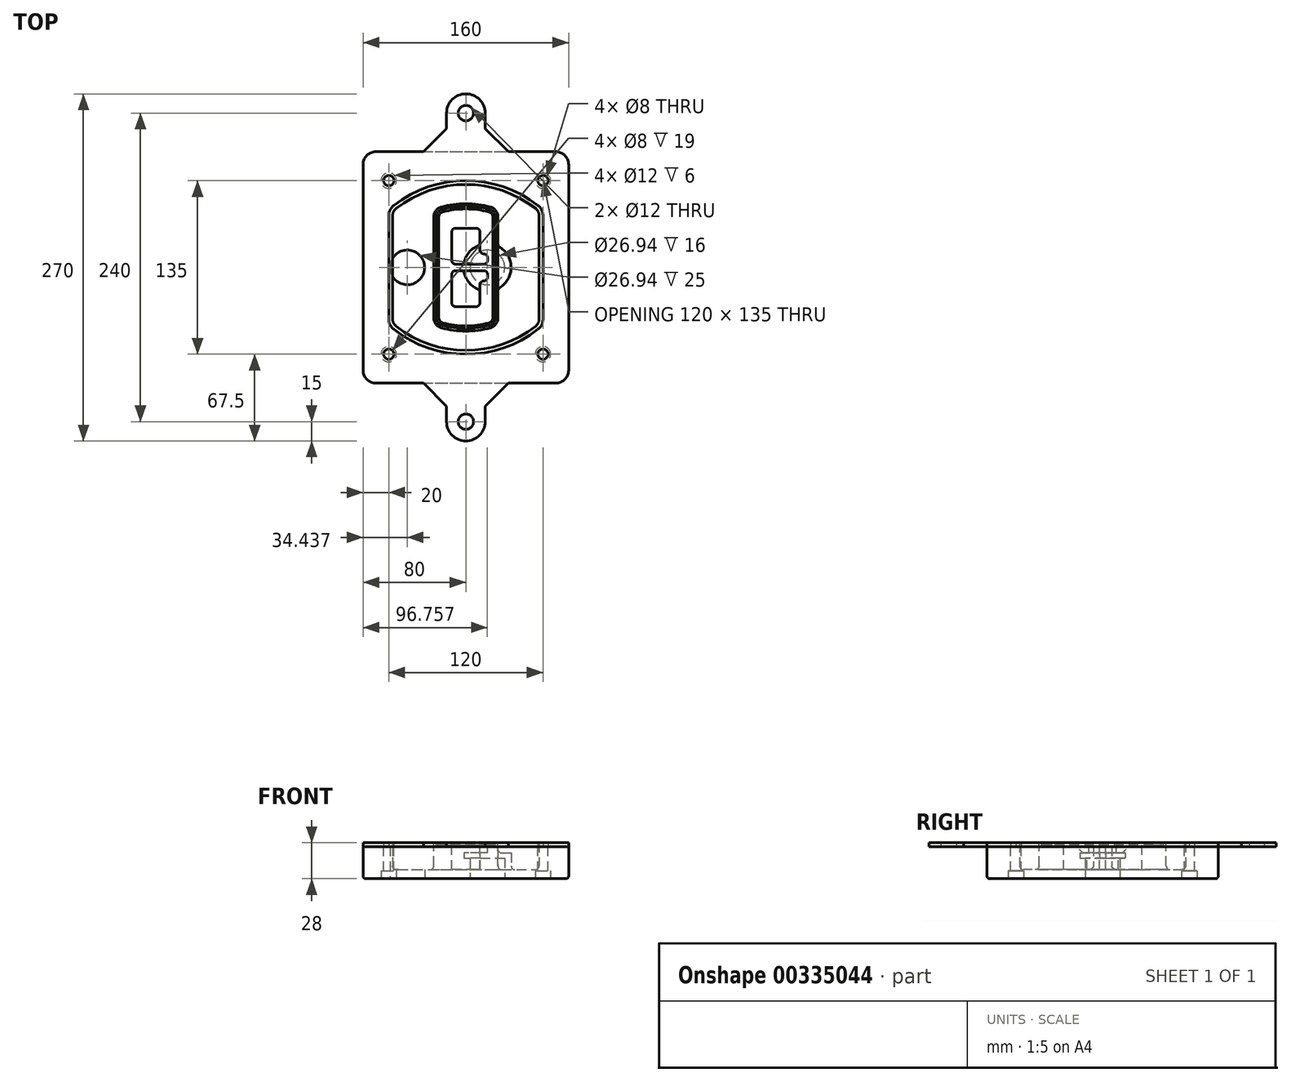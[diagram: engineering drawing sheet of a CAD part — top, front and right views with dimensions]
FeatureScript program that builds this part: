
annotation { "Feature Type Name" : "Feature", "Feature Type Description" : "" }
export const myFeature = defineFeature(function(context is Context, id is Id, definition is map)
    precondition{}
    {
        {
            var Q0;
            Q0=qCreatedBy(makeId("Top.planeOp"),FACE);
            var sketch = newSketch(context, id + "F0", { "sketchPlane" : qUnion([Q0])});
            skPoint(sketch, "E0.rect.middle", {"position": v(0, 0) * mm});
            skLineSegment(sketch, "E1.bottom", {"start": v(-70, -90) * mm, "end": v(70, -90) * mm});
            skLineSegment(sketch, "E1.top", {"start": v(-70, 90) * mm, "end": v(70, 90) * mm});
            skLineSegment(sketch, "E1.left", {"start": v(-80, -80) * mm, "end": v(-80, 80) * mm});
            skLineSegment(sketch, "E1.right", {"start": v(80, -80) * mm, "end": v(80, 80) * mm});
            skLineSegment(sketch, "E2", {"start": v(-80, 90) * mm, "end": v(80, -90) * mm, "construction": true});
            skLineSegment(sketch, "E3", {"start": v(80, 90) * mm, "end": v(-80, -90) * mm, "construction": true});
            skCircle(sketch, "E4", {"center": v(-60, 67.5) * mm, "radius": 4 * mm});
            skCircle(sketch, "E5", {"center": v(60, 67.5) * mm, "radius": 4 * mm});
            skCircle(sketch, "E6", {"center": v(60, -67.5) * mm, "radius": 4 * mm});
            skCircle(sketch, "E7", {"center": v(-60, -67.5) * mm, "radius": 4 * mm});
            skLineSegment(sketch, "E8", {"start": v(-60, 67.5) * mm, "end": v(60, 67.5) * mm, "construction": true});
            skLineSegment(sketch, "E9", {"start": v(60, 67.5) * mm, "end": v(60, -67.5) * mm, "construction": true});
            skLineSegment(sketch, "E10", {"start": v(60, -67.5) * mm, "end": v(-60, -67.5) * mm, "construction": true});
            skLineSegment(sketch, "E11", {"start": v(-60, -67.5) * mm, "end": v(-60, 67.5) * mm, "construction": true});
            skLineSegment(sketch, "E12", {"start": v(-60, 40.3) * mm, "end": v(-60, -40.3) * mm});
            skLineSegment(sketch, "E13", {"start": v(60, 40.3) * mm, "end": v(60, -40.3) * mm});
            skArc(sketch, "E14", {"start": v(56.15, 48.18) * mm, "mid": v(0, 67.5) * mm, "end": v(-56.15, 48.18) * mm});
            skArc(sketch, "E15", {"start": v(-56.15, -48.18) * mm, "mid": v(0, -67.5) * mm, "end": v(56.15, -48.18) * mm});
            skLineSegment(sketch, "E16", {"start": v(-60, 0) * mm, "end": v(60, 0) * mm, "construction": true});
            skPoint(sketch, "E17.visualSharp", {"position": v(-60, -45) * mm});
            skArc(sketch, "E17.filletArc", {"start": v(-60, -40.3) * mm, "mid": v(-58.99, -44.68) * mm, "end": v(-56.15, -48.18) * mm});
            skPoint(sketch, "E18.visualSharp", {"position": v(-60, 45) * mm});
            skArc(sketch, "E18.filletArc", {"start": v(-56.15, 48.18) * mm, "mid": v(-58.99, 44.68) * mm, "end": v(-60, 40.3) * mm});
            skPoint(sketch, "E19.visualSharp", {"position": v(60, 45) * mm});
            skArc(sketch, "E19.filletArc", {"start": v(60, 40.3) * mm, "mid": v(58.99, 44.68) * mm, "end": v(56.15, 48.18) * mm});
            skPoint(sketch, "E20.visualSharp", {"position": v(60, -45) * mm});
            skArc(sketch, "E20.filletArc", {"start": v(56.15, -48.18) * mm, "mid": v(58.99, -44.68) * mm, "end": v(60, -40.3) * mm});
            skPoint(sketch, "E21.visualSharp", {"position": v(-80, 90) * mm});
            skArc(sketch, "E21.filletArc", {"start": v(-70, 90) * mm, "mid": v(-77.07, 87.07) * mm, "end": v(-80, 80) * mm});
            skPoint(sketch, "E22.visualSharp", {"position": v(80, 90) * mm});
            skArc(sketch, "E22.filletArc", {"start": v(80, 80) * mm, "mid": v(77.07, 87.07) * mm, "end": v(70, 90) * mm});
            skPoint(sketch, "E23.visualSharp", {"position": v(80, -90) * mm});
            skArc(sketch, "E23.filletArc", {"start": v(70, -90) * mm, "mid": v(77.07, -87.07) * mm, "end": v(80, -80) * mm});
            skPoint(sketch, "E24.visualSharp", {"position": v(-80, -90) * mm});
            skArc(sketch, "E24.filletArc", {"start": v(-80, -80) * mm, "mid": v(-77.07, -87.07) * mm, "end": v(-70, -90) * mm});
            skArc(sketch, "E25.0", {"start": v(57, 40.3) * mm, "mid": v(56.3, 43.36) * mm, "end": v(54.3, 45.81) * mm});
            skLineSegment(sketch, "E25.1", {"start": v(57, 40.3) * mm, "end": v(57, -40.3) * mm});
            skArc(sketch, "E25.2", {"start": v(54.3, -45.81) * mm, "mid": v(56.3, -43.36) * mm, "end": v(57, -40.3) * mm});
            skArc(sketch, "E25.3", {"start": v(-54.3, -45.81) * mm, "mid": v(0, -64.5) * mm, "end": v(54.3, -45.81) * mm});
            skArc(sketch, "E25.4", {"start": v(-57, -40.3) * mm, "mid": v(-56.3, -43.36) * mm, "end": v(-54.3, -45.81) * mm});
            skArc(sketch, "E25.5", {"start": v(54.3, 45.81) * mm, "mid": v(0, 64.5) * mm, "end": v(-54.3, 45.81) * mm});
            skLineSegment(sketch, "E25.6", {"start": v(-57, 40.3) * mm, "end": v(-57, -40.3) * mm});
            skArc(sketch, "E25.7", {"start": v(-54.3, 45.81) * mm, "mid": v(-56.3, 43.36) * mm, "end": v(-57, 40.3) * mm});
            skArc(sketch, "E26.0", {"start": v(-58.62, 51.33) * mm, "mid": v(-62.58, 46.43) * mm, "end": v(-64, 40.3) * mm});
            skArc(sketch, "E26.1", {"start": v(58.62, 51.33) * mm, "mid": v(0, 71.5) * mm, "end": v(-58.62, 51.33) * mm});
            skArc(sketch, "E26.2", {"start": v(64, 40.3) * mm, "mid": v(62.58, 46.43) * mm, "end": v(58.62, 51.33) * mm});
            skLineSegment(sketch, "E26.3", {"start": v(64, 40.3) * mm, "end": v(64, -40.3) * mm});
            skArc(sketch, "E26.4", {"start": v(58.62, -51.33) * mm, "mid": v(62.58, -46.43) * mm, "end": v(64, -40.3) * mm});
            skLineSegment(sketch, "E26.5", {"start": v(-64, 40.3) * mm, "end": v(-64, -40.3) * mm});
            skArc(sketch, "E26.6", {"start": v(-58.62, -51.33) * mm, "mid": v(0, -71.5) * mm, "end": v(58.62, -51.33) * mm});
            skArc(sketch, "E26.7", {"start": v(-64, -40.3) * mm, "mid": v(-62.58, -46.43) * mm, "end": v(-58.62, -51.33) * mm});
            skSolve(sketch);
        }
        {
            var Q0;
            Q0=makeQuery(id+"F0.imprint","IMPRINT",FACE,{"disambiguationData":[TD([[makeQuery(id+"F0.imprint","IMPRINT",EDGE,{"derivedFrom":sQuery(id+"F0.wireOp",EDGE,"E1.bottom")}),1.0]])]});
            var Q1;
            Q1=makeQuery(id+"F0.imprint","IMPRINT",FACE,{"disambiguationData":[TD([[makeQuery(id+"F0.imprint","IMPRINT",EDGE,{"derivedFrom":sQuery(id+"F0.wireOp",EDGE,"E12")}),1.0]])]});
            var Q2;
            Q2=makeQuery(id+"F0.imprint","IMPRINT",FACE,{"disambiguationData":[TD([[makeQuery(id+"F0.imprint","IMPRINT",EDGE,{"derivedFrom":sQuery(id+"F0.wireOp",EDGE,"E25.0")}),1.0]])]});
            var Q3;
            Q3=makeQuery(id+"F0.imprint","IMPRINT",FACE,{"disambiguationData":[TD([[makeQuery(id+"F0.imprint","IMPRINT",EDGE,{"derivedFrom":sQuery(id+"F0.wireOp",EDGE,"E12")}),-1.0]])]});
            extrude(context, id + "F1", {"entities" : qUnion([Q0, Q1, Q2, Q3]), "oppositeDirection" : true, "depth" : 25 * mm});
        }
        {
            var Q0;
            Q0=makeQuery(id+"F0.imprint","IMPRINT",FACE,{"disambiguationData":[TD([[makeQuery(id+"F0.imprint","IMPRINT",EDGE,{"derivedFrom":sQuery(id+"F0.wireOp",EDGE,"E12")}),1.0]])]});
            extrude(context, id + "F2", {"entities" : qUnion([Q0]), "operationType" : NewBodyOperationType.ADD, "depth" : 3 * mm});
        }
        {
            var Q0;
            Q0=makeQuery(id+"F0.imprint","IMPRINT",FACE,{"disambiguationData":[TD([[makeQuery(id+"F0.imprint","IMPRINT",EDGE,{"derivedFrom":sQuery(id+"F0.wireOp",EDGE,"E25.0")}),1.0]])]});
            extrude(context, id + "F3", {"entities" : qUnion([Q0]), "operationType" : NewBodyOperationType.REMOVE, "oppositeDirection" : true, "depth" : 18 * mm});
        }
        {
            var Q0;
            Q0=makeQuery(id+"F2.opExtrude","CAP_FACE",FACE,{"disambiguationData":[OSD([sQuery(id+"F0.wireOp",EDGE,"E12"),sQuery(id+"F0.wireOp",EDGE,"E13"),sQuery(id+"F0.wireOp",EDGE,"E14"),sQuery(id+"F0.wireOp",EDGE,"E15"),sQuery(id+"F0.wireOp",EDGE,"E17.filletArc"),sQuery(id+"F0.wireOp",EDGE,"E18.filletArc"),sQuery(id+"F0.wireOp",EDGE,"E19.filletArc"),sQuery(id+"F0.wireOp",EDGE,"E20.filletArc"),sQuery(id+"F0.wireOp",EDGE,"E25.0"),sQuery(id+"F0.wireOp",EDGE,"E25.1"),sQuery(id+"F0.wireOp",EDGE,"E25.2"),sQuery(id+"F0.wireOp",EDGE,"E25.3"),sQuery(id+"F0.wireOp",EDGE,"E25.4"),sQuery(id+"F0.wireOp",EDGE,"E25.5"),sQuery(id+"F0.wireOp",EDGE,"E25.6"),sQuery(id+"F0.wireOp",EDGE,"E25.7")])],"isStart":false});
            var sketch = newSketch(context, id + "F4", { "sketchPlane" : qUnion([Q0])});
            skArc(sketch, "E27.0", {"start": v(-19.08, -46.97) * mm, "mid": v(0, -49.5) * mm, "end": v(19.08, -46.97) * mm});
            skArc(sketch, "E28.0", {"start": v(19.08, 46.97) * mm, "mid": v(0, 49.5) * mm, "end": v(-19.08, 46.97) * mm});
            skLineSegment(sketch, "E29", {"start": v(-25, 39.25) * mm, "end": v(-25, -39.25) * mm});
            skLineSegment(sketch, "E30", {"start": v(25, 39.25) * mm, "end": v(25, -39.25) * mm});
            skLineSegment(sketch, "E31", {"start": v(-25, 45.1) * mm, "end": v(25, 45.1) * mm, "construction": true});
            skLineSegment(sketch, "E32", {"start": v(-25, -45.1) * mm, "end": v(25, -45.1) * mm, "construction": true});
            skPoint(sketch, "E33.visualSharp", {"position": v(-25, 45.1) * mm});
            skArc(sketch, "E33.filletArc", {"start": v(-19.08, 46.97) * mm, "mid": v(-23.35, 44.11) * mm, "end": v(-25, 39.25) * mm});
            skPoint(sketch, "E34.visualSharp", {"position": v(25, 45.1) * mm});
            skArc(sketch, "E34.filletArc", {"start": v(25, 39.25) * mm, "mid": v(23.35, 44.11) * mm, "end": v(19.08, 46.97) * mm});
            skPoint(sketch, "E35.visualSharp", {"position": v(25, -45.1) * mm});
            skArc(sketch, "E35.filletArc", {"start": v(19.08, -46.97) * mm, "mid": v(23.35, -44.11) * mm, "end": v(25, -39.25) * mm});
            skPoint(sketch, "E36.visualSharp", {"position": v(-25, -45.1) * mm});
            skArc(sketch, "E36.filletArc", {"start": v(-25, -39.25) * mm, "mid": v(-23.35, -44.11) * mm, "end": v(-19.08, -46.97) * mm});
            skArc(sketch, "E37.0", {"start": v(54.3, 45.81) * mm, "mid": v(0, 64.5) * mm, "end": v(-54.3, 45.81) * mm});
            skArc(sketch, "E37.1", {"start": v(-54.3, 45.81) * mm, "mid": v(-56.3, 43.36) * mm, "end": v(-57, 40.3) * mm});
            skLineSegment(sketch, "E37.2", {"start": v(-57, 40.3) * mm, "end": v(-57, -40.3) * mm});
            skArc(sketch, "E37.3", {"start": v(-57, -40.3) * mm, "mid": v(-56.3, -43.36) * mm, "end": v(-54.3, -45.81) * mm});
            skArc(sketch, "E37.4", {"start": v(-54.3, -45.81) * mm, "mid": v(0, -64.5) * mm, "end": v(54.3, -45.81) * mm});
            skArc(sketch, "E37.5", {"start": v(54.3, -45.81) * mm, "mid": v(56.3, -43.36) * mm, "end": v(57, -40.3) * mm});
            skLineSegment(sketch, "E37.6", {"start": v(57, 40.3) * mm, "end": v(57, -40.3) * mm});
            skArc(sketch, "E37.7", {"start": v(57, 40.3) * mm, "mid": v(56.3, 43.36) * mm, "end": v(54.3, 45.81) * mm});
            skLineSegment(sketch, "E38.0", {"start": v(23, 39.25) * mm, "end": v(23, -39.25) * mm});
            skArc(sketch, "E38.1", {"start": v(18.56, -45.04) * mm, "mid": v(21.76, -42.9) * mm, "end": v(23, -39.25) * mm});
            skArc(sketch, "E38.2", {"start": v(-18.56, -45.04) * mm, "mid": v(0, -47.5) * mm, "end": v(18.56, -45.04) * mm});
            skArc(sketch, "E38.3", {"start": v(-23, -39.25) * mm, "mid": v(-21.76, -42.9) * mm, "end": v(-18.56, -45.04) * mm});
            skLineSegment(sketch, "E38.4", {"start": v(-23, 39.25) * mm, "end": v(-23, -39.25) * mm});
            skArc(sketch, "E38.5", {"start": v(23, 39.25) * mm, "mid": v(21.76, 42.9) * mm, "end": v(18.56, 45.04) * mm});
            skArc(sketch, "E38.6", {"start": v(-18.56, 45.04) * mm, "mid": v(-21.76, 42.9) * mm, "end": v(-23, 39.25) * mm});
            skArc(sketch, "E38.7", {"start": v(18.56, 45.04) * mm, "mid": v(0, 47.5) * mm, "end": v(-18.56, 45.04) * mm});
            skArc(sketch, "E39.0", {"start": v(21, 39.25) * mm, "mid": v(20.18, 41.68) * mm, "end": v(18.04, 43.1) * mm});
            skLineSegment(sketch, "E39.1", {"start": v(21, 39.25) * mm, "end": v(21, -39.25) * mm});
            skArc(sketch, "E39.2", {"start": v(18.04, -43.1) * mm, "mid": v(20.18, -41.68) * mm, "end": v(21, -39.25) * mm});
            skArc(sketch, "E39.3", {"start": v(-18.04, -43.1) * mm, "mid": v(0, -45.5) * mm, "end": v(18.04, -43.1) * mm});
            skArc(sketch, "E39.4", {"start": v(-21, -39.25) * mm, "mid": v(-20.18, -41.68) * mm, "end": v(-18.04, -43.1) * mm});
            skArc(sketch, "E39.5", {"start": v(18.04, 43.1) * mm, "mid": v(0, 45.5) * mm, "end": v(-18.04, 43.1) * mm});
            skLineSegment(sketch, "E39.6", {"start": v(-21, 39.25) * mm, "end": v(-21, -39.25) * mm});
            skArc(sketch, "E39.7", {"start": v(-18.04, 43.1) * mm, "mid": v(-20.18, 41.68) * mm, "end": v(-21, 39.25) * mm});
            skLineSegment(sketch, "E40", {"start": v(-25, 0) * mm, "end": v(25, 0) * mm, "construction": true});
            skLineSegment(sketch, "E41", {"start": v(-11, 5.5) * mm, "end": v(-11, 27.5) * mm});
            skLineSegment(sketch, "E42", {"start": v(-8, 30.5) * mm, "end": v(8, 30.5) * mm});
            skLineSegment(sketch, "E43", {"start": v(11, 27.5) * mm, "end": v(11, 13.5) * mm});
            skLineSegment(sketch, "E44", {"start": v(14, 10.5) * mm, "end": v(14, 10.5) * mm});
            skLineSegment(sketch, "E45", {"start": v(17, 7.5) * mm, "end": v(17, 5.5) * mm});
            skLineSegment(sketch, "E46", {"start": v(14, 2.5) * mm, "end": v(-8, 2.5) * mm});
            skPoint(sketch, "E47.visualSharp", {"position": v(-11, 30.5) * mm});
            skArc(sketch, "E47.filletArc", {"start": v(-8, 30.5) * mm, "mid": v(-10.12, 29.62) * mm, "end": v(-11, 27.5) * mm});
            skPoint(sketch, "E48.visualSharp", {"position": v(11, 30.5) * mm});
            skArc(sketch, "E48.filletArc", {"start": v(11, 27.5) * mm, "mid": v(10.12, 29.62) * mm, "end": v(8, 30.5) * mm});
            skPoint(sketch, "E49.visualSharp", {"position": v(11, 10.5) * mm});
            skArc(sketch, "E49.filletArc", {"start": v(11, 13.5) * mm, "mid": v(11.88, 11.38) * mm, "end": v(14, 10.5) * mm});
            skPoint(sketch, "E50.visualSharp", {"position": v(17, 10.5) * mm});
            skArc(sketch, "E50.filletArc", {"start": v(17, 7.5) * mm, "mid": v(16.12, 9.62) * mm, "end": v(14, 10.5) * mm});
            skPoint(sketch, "E51.visualSharp", {"position": v(17, 2.5) * mm});
            skArc(sketch, "E51.filletArc", {"start": v(14, 2.5) * mm, "mid": v(16.12, 3.38) * mm, "end": v(17, 5.5) * mm});
            skPoint(sketch, "E52.visualSharp", {"position": v(-11, 2.5) * mm});
            skArc(sketch, "E52.filletArc", {"start": v(-11, 5.5) * mm, "mid": v(-10.12, 3.38) * mm, "end": v(-8, 2.5) * mm});
            skLineSegment(sketch, "E53.0.MirrorCS", {"start": v(14, -2.5) * mm, "end": v(-8, -2.5) * mm});
            skArc(sketch, "E54.0.MirrorCS", {"start": v(-11, -5.5) * mm, "mid": v(-10.12, -3.38) * mm, "end": v(-8, -2.5) * mm});
            skLineSegment(sketch, "E55.0.MirrorCS", {"start": v(-11, -5.5) * mm, "end": v(-11, -27.5) * mm});
            skArc(sketch, "E56.0.MirrorCS", {"start": v(-8, -30.5) * mm, "mid": v(-10.12, -29.62) * mm, "end": v(-11, -27.5) * mm});
            skLineSegment(sketch, "E57.0.MirrorCS", {"start": v(-8, -30.5) * mm, "end": v(8, -30.5) * mm});
            skArc(sketch, "E58.0.MirrorCS", {"start": v(11, -27.5) * mm, "mid": v(10.12, -29.62) * mm, "end": v(8, -30.5) * mm});
            skLineSegment(sketch, "E59.0.MirrorCS", {"start": v(11, -27.5) * mm, "end": v(11, -13.5) * mm});
            skArc(sketch, "E60.0.MirrorCS", {"start": v(11, -13.5) * mm, "mid": v(11.88, -11.38) * mm, "end": v(14, -10.5) * mm});
            skArc(sketch, "E61.0.MirrorCS", {"start": v(17, -7.5) * mm, "mid": v(16.12, -9.62) * mm, "end": v(14, -10.5) * mm});
            skLineSegment(sketch, "E62.0.MirrorCS", {"start": v(17, -7.5) * mm, "end": v(17, -5.5) * mm});
            skArc(sketch, "E63.0.MirrorCS", {"start": v(14, -2.5) * mm, "mid": v(16.12, -3.38) * mm, "end": v(17, -5.5) * mm});
            skSolve(sketch);
        }
        {
            var Q0;
            Q0=makeQuery(id+"F4.imprint","IMPRINT",FACE,{"disambiguationData":[TD([[makeQuery(id+"F4.imprint","IMPRINT",EDGE,{"derivedFrom":sQuery(id+"F4.wireOp",EDGE,"E27.0")}),1.0]])]});
            var Q1;
            Q1=makeQuery(id+"F4.imprint","IMPRINT",FACE,{"disambiguationData":[TD([[makeQuery(id+"F4.imprint","IMPRINT",EDGE,{"derivedFrom":sQuery(id+"F4.wireOp",EDGE,"E38.0")}),-1.0]])]});
            var Q2;
            Q2=makeQuery(id+"F4.imprint","IMPRINT",FACE,{"disambiguationData":[TD([[makeQuery(id+"F4.imprint","IMPRINT",EDGE,{"derivedFrom":sQuery(id+"F4.wireOp",EDGE,"E39.0")}),1.0]])]});
            extrude(context, id + "F5", {"entities" : qUnion([Q0, Q1, Q2]), "operationType" : NewBodyOperationType.ADD, "endBound" : BoundingType.UP_TO_NEXT, "oppositeDirection" : true, "depth" : 25 * mm});
        }
        {
            var Q0;
            Q0=makeQuery(id+"F4.imprint","IMPRINT",FACE,{"disambiguationData":[TD([[makeQuery(id+"F4.imprint","IMPRINT",EDGE,{"derivedFrom":sQuery(id+"F4.wireOp",EDGE,"E38.0")}),-1.0]])]});
            extrude(context, id + "F6", {"entities" : qUnion([Q0]), "operationType" : NewBodyOperationType.REMOVE, "oppositeDirection" : true, "depth" : 2 * mm});
        }
        {
            var Q0;
            Q0=makeQuery(id+"F1.opExtrude","CAP_FACE",FACE,{"disambiguationData":[OSD([sQuery(id+"F0.wireOp",EDGE,"E1.bottom"),sQuery(id+"F0.wireOp",EDGE,"E1.top"),sQuery(id+"F0.wireOp",EDGE,"E1.left"),sQuery(id+"F0.wireOp",EDGE,"E1.right"),sQuery(id+"F0.wireOp",EDGE,"E4"),sQuery(id+"F0.wireOp",EDGE,"E5"),sQuery(id+"F0.wireOp",EDGE,"E6"),sQuery(id+"F0.wireOp",EDGE,"E7"),sQuery(id+"F0.wireOp",EDGE,"E21.filletArc"),sQuery(id+"F0.wireOp",EDGE,"E22.filletArc"),sQuery(id+"F0.wireOp",EDGE,"E23.filletArc"),sQuery(id+"F0.wireOp",EDGE,"E24.filletArc")])],"isStart":false});
            var sketch = newSketch(context, id + "F7", { "sketchPlane" : qUnion([Q0])});
            skCircle(sketch, "E64", {"center": v(16.76, 0) * mm, "radius": 13.47 * mm});
            skCircle(sketch, "E65", {"center": v(-45.56, 0) * mm, "radius": 13.47 * mm});
            skLineSegment(sketch, "E66", {"start": v(80, 0) * mm, "end": v(-80, 0) * mm});
            skCircle(sketch, "E67", {"center": v(16.76, 0) * mm, "radius": 18.47 * mm});
            skCircle(sketch, "E68", {"center": v(60, -67.5) * mm, "radius": 6 * mm});
            skCircle(sketch, "E69", {"center": v(-60, -67.5) * mm, "radius": 6 * mm});
            skCircle(sketch, "E70", {"center": v(-60, 67.5) * mm, "radius": 6 * mm});
            skCircle(sketch, "E71", {"center": v(60, 67.5) * mm, "radius": 6 * mm});
            skSolve(sketch);
        }
        {
            var Q0;
            {var subQ1=sQuery(id+"F7.wireOp",EDGE,"E66");var subQ4=sQuery(id+"F7.wireOp",EDGE,"E64");var subQ6=makeQuery(id+"F7.imprint","INTERSECT",VERTEX,{"disambiguationData":[OD(0.0)],"derivedFrom":[subQ4,subQ1]});Q0=makeQuery(id+"F7.imprint","IMPRINT",FACE,{"disambiguationData":[TD([[makeQuery(id+"F7.imprint","IMPRINT",EDGE,{"disambiguationData":[TD([[subQ6,-1.0]])],"derivedFrom":subQ4}),-1.0]])]});}
            var Q1;
            {var subQ0=sQuery(id+"F7.wireOp",EDGE,"E66");var subQ1=sQuery(id+"F7.wireOp",EDGE,"E64");var subQ3=makeQuery(id+"F7.imprint","INTERSECT",VERTEX,{"disambiguationData":[OD(0.0)],"derivedFrom":[subQ1,subQ0]});Q1=makeQuery(id+"F7.imprint","IMPRINT",FACE,{"disambiguationData":[TD([[makeQuery(id+"F7.imprint","IMPRINT",EDGE,{"disambiguationData":[TD([[subQ3,-1.0]])],"derivedFrom":subQ1}),1.0]])]});}
            var Q2;
            {var subQ0=sQuery(id+"F7.wireOp",EDGE,"E66");var subQ1=sQuery(id+"F7.wireOp",EDGE,"E64");var subQ3=makeQuery(id+"F7.imprint","INTERSECT",VERTEX,{"disambiguationData":[OD(0.0)],"derivedFrom":[subQ1,subQ0]});Q2=makeQuery(id+"F7.imprint","IMPRINT",FACE,{"disambiguationData":[TD([[makeQuery(id+"F7.imprint","IMPRINT",EDGE,{"disambiguationData":[TD([[subQ3,1.0]])],"derivedFrom":subQ1}),1.0]])]});}
            var Q3;
            {var subQ1=sQuery(id+"F7.wireOp",EDGE,"E66");var subQ4=sQuery(id+"F7.wireOp",EDGE,"E64");var subQ6=makeQuery(id+"F7.imprint","INTERSECT",VERTEX,{"disambiguationData":[OD(0.0)],"derivedFrom":[subQ4,subQ1]});Q3=makeQuery(id+"F7.imprint","IMPRINT",FACE,{"disambiguationData":[TD([[makeQuery(id+"F7.imprint","IMPRINT",EDGE,{"disambiguationData":[TD([[subQ6,1.0]])],"derivedFrom":subQ4}),-1.0]])]});}
            extrude(context, id + "F8", {"entities" : qUnion([Q0, Q1, Q2, Q3]), "operationType" : NewBodyOperationType.ADD, "oppositeDirection" : true, "depth" : 20 * mm});
        }
        {
            var Q0;
            {var subQ0=sQuery(id+"F7.wireOp",EDGE,"E66");var subQ1=sQuery(id+"F7.wireOp",EDGE,"E64");var subQ3=makeQuery(id+"F7.imprint","INTERSECT",VERTEX,{"disambiguationData":[OD(0.0)],"derivedFrom":[subQ1,subQ0]});Q0=makeQuery(id+"F7.imprint","IMPRINT",FACE,{"disambiguationData":[TD([[makeQuery(id+"F7.imprint","IMPRINT",EDGE,{"disambiguationData":[TD([[subQ3,-1.0]])],"derivedFrom":subQ1}),1.0]])]});}
            var Q1;
            {var subQ0=sQuery(id+"F7.wireOp",EDGE,"E66");var subQ1=sQuery(id+"F7.wireOp",EDGE,"E64");var subQ3=makeQuery(id+"F7.imprint","INTERSECT",VERTEX,{"disambiguationData":[OD(0.0)],"derivedFrom":[subQ1,subQ0]});Q1=makeQuery(id+"F7.imprint","IMPRINT",FACE,{"disambiguationData":[TD([[makeQuery(id+"F7.imprint","IMPRINT",EDGE,{"disambiguationData":[TD([[subQ3,1.0]])],"derivedFrom":subQ1}),1.0]])]});}
            extrude(context, id + "F9", {"entities" : qUnion([Q0, Q1]), "operationType" : NewBodyOperationType.REMOVE, "oppositeDirection" : true, "depth" : 16 * mm});
        }
        {
            var Q0;
            {var subQ0=sQuery(id+"F7.wireOp",EDGE,"E66");var subQ1=sQuery(id+"F7.wireOp",EDGE,"E65");var subQ3=makeQuery(id+"F7.imprint","INTERSECT",VERTEX,{"disambiguationData":[OD(0.0)],"derivedFrom":[subQ1,subQ0]});Q0=makeQuery(id+"F7.imprint","IMPRINT",FACE,{"disambiguationData":[TD([[makeQuery(id+"F7.imprint","IMPRINT",EDGE,{"disambiguationData":[TD([[subQ3,-1.0]])],"derivedFrom":subQ1}),1.0]])]});}
            var Q1;
            {var subQ0=sQuery(id+"F7.wireOp",EDGE,"E66");var subQ1=sQuery(id+"F7.wireOp",EDGE,"E65");var subQ3=makeQuery(id+"F7.imprint","INTERSECT",VERTEX,{"disambiguationData":[OD(0.0)],"derivedFrom":[subQ1,subQ0]});Q1=makeQuery(id+"F7.imprint","IMPRINT",FACE,{"disambiguationData":[TD([[makeQuery(id+"F7.imprint","IMPRINT",EDGE,{"disambiguationData":[TD([[subQ3,1.0]])],"derivedFrom":subQ1}),1.0]])]});}
            extrude(context, id + "F10", {"entities" : qUnion([Q0, Q1]), "operationType" : NewBodyOperationType.REMOVE, "oppositeDirection" : true, "depth" : 25 * mm});
        }
        {
            var Q0;
            Q0=makeQuery(id+"F7.imprint","IMPRINT",FACE,{"disambiguationData":[TD([[makeQuery(id+"F7.imprint","IMPRINT",EDGE,{"derivedFrom":sQuery(id+"F7.wireOp",EDGE,"E68")}),1.0]])]});
            var Q1;
            Q1=makeQuery(id+"F7.imprint","IMPRINT",FACE,{"disambiguationData":[TD([[makeQuery(id+"F7.imprint","IMPRINT",EDGE,{"derivedFrom":makeQuery(id+"F1.opExtrude","CAP_EDGE",EDGE,{"disambiguationData":[OSD([sQuery(id+"F0.wireOp",EDGE,"E5")])],"isStart":false})}),-1.0]])]});
            var Q2;
            Q2=makeQuery(id+"F7.imprint","IMPRINT",FACE,{"disambiguationData":[TD([[makeQuery(id+"F7.imprint","IMPRINT",EDGE,{"derivedFrom":sQuery(id+"F7.wireOp",EDGE,"E69")}),1.0]])]});
            var Q3;
            Q3=makeQuery(id+"F7.imprint","IMPRINT",FACE,{"disambiguationData":[TD([[makeQuery(id+"F7.imprint","IMPRINT",EDGE,{"derivedFrom":makeQuery(id+"F1.opExtrude","CAP_EDGE",EDGE,{"disambiguationData":[OSD([sQuery(id+"F0.wireOp",EDGE,"E4")])],"isStart":false})}),-1.0]])]});
            var Q4;
            Q4=makeQuery(id+"F7.imprint","IMPRINT",FACE,{"disambiguationData":[TD([[makeQuery(id+"F7.imprint","IMPRINT",EDGE,{"derivedFrom":sQuery(id+"F7.wireOp",EDGE,"E70")}),1.0]])]});
            var Q5;
            Q5=makeQuery(id+"F7.imprint","IMPRINT",FACE,{"disambiguationData":[TD([[makeQuery(id+"F7.imprint","IMPRINT",EDGE,{"derivedFrom":makeQuery(id+"F1.opExtrude","CAP_EDGE",EDGE,{"disambiguationData":[OSD([sQuery(id+"F0.wireOp",EDGE,"E7")])],"isStart":false})}),-1.0]])]});
            var Q6;
            Q6=makeQuery(id+"F7.imprint","IMPRINT",FACE,{"disambiguationData":[TD([[makeQuery(id+"F7.imprint","IMPRINT",EDGE,{"derivedFrom":sQuery(id+"F7.wireOp",EDGE,"E71")}),1.0]])]});
            var Q7;
            Q7=makeQuery(id+"F7.imprint","IMPRINT",FACE,{"disambiguationData":[TD([[makeQuery(id+"F7.imprint","IMPRINT",EDGE,{"derivedFrom":makeQuery(id+"F1.opExtrude","CAP_EDGE",EDGE,{"disambiguationData":[OSD([sQuery(id+"F0.wireOp",EDGE,"E6")])],"isStart":false})}),-1.0]])]});
            extrude(context, id + "F11", {"entities" : qUnion([Q0, Q1, Q2, Q3, Q4, Q5, Q6, Q7]), "operationType" : NewBodyOperationType.REMOVE, "oppositeDirection" : true, "depth" : 6 * mm});
        }
        {
            var Q0;
            Q0=makeQuery(id+"F9.boolean.opBoolean","COPY",FACE,{"derivedFrom":makeQuery(id+"F9.opExtrude","CAP_FACE",FACE,{"disambiguationData":[OSD([sQuery(id+"F7.wireOp",EDGE,"E64")])],"isStart":false})});
            var sketch = newSketch(context, id + "F12", { "sketchPlane" : qUnion([Q0])});
            skArc(sketch, "E72.0", {"start": v(11, 17.55) * mm, "mid": v(2.57, 11.82) * mm, "end": v(-1.54, 2.5) * mm});
            skArc(sketch, "E72.1", {"start": v(-1.54, -2.5) * mm, "mid": v(2.57, -11.82) * mm, "end": v(11, -17.55) * mm});
            skLineSegment(sketch, "E73", {"start": v(-1.54, -2.5) * mm, "end": v(14, -2.5) * mm});
            skLineSegment(sketch, "E74.0", {"start": v(14, 2.5) * mm, "end": v(-1.54, 2.5) * mm});
            skArc(sketch, "E74.1", {"start": v(14, 2.5) * mm, "mid": v(16.12, 3.38) * mm, "end": v(17, 5.5) * mm});
            skLineSegment(sketch, "E74.2", {"start": v(17, 7.5) * mm, "end": v(17, 5.5) * mm});
            skArc(sketch, "E74.3", {"start": v(17, 7.5) * mm, "mid": v(16.12, 9.62) * mm, "end": v(14, 10.5) * mm});
            skArc(sketch, "E74.4", {"start": v(11, 13.5) * mm, "mid": v(11.88, 11.38) * mm, "end": v(14, 10.5) * mm});
            skLineSegment(sketch, "E74.5", {"start": v(11, 17.55) * mm, "end": v(11, 13.5) * mm});
            skLineSegment(sketch, "E74.7", {"start": v(14, -2.5) * mm, "end": v(-1.54, -2.5) * mm});
            skArc(sketch, "E74.8", {"start": v(14, -2.5) * mm, "mid": v(16.12, -3.38) * mm, "end": v(17, -5.5) * mm});
            skLineSegment(sketch, "E74.9", {"start": v(17, -7.5) * mm, "end": v(17, -5.5) * mm});
            skArc(sketch, "E74.10", {"start": v(17, -7.5) * mm, "mid": v(16.12, -9.62) * mm, "end": v(14, -10.5) * mm});
            skArc(sketch, "E74.11", {"start": v(11, -13.5) * mm, "mid": v(11.88, -11.38) * mm, "end": v(14, -10.5) * mm});
            skLineSegment(sketch, "E74.12", {"start": v(11, -17.55) * mm, "end": v(11, -13.5) * mm});
            skPoint(sketch, "E75.orphan", {"position": v(11, -27.5) * mm});
            skPoint(sketch, "E76.orphan", {"position": v(-8, -2.5) * mm});
            skPoint(sketch, "E77.orphan", {"position": v(-8, 2.5) * mm});
            skPoint(sketch, "E78.orphan", {"position": v(11, 27.5) * mm});
            skSolve(sketch);
        }
        {
            var Q0;
            {var subQ7=sQuery(id+"F12.wireOp",EDGE,"E72.0");var subQ14=sQuery(id+"F12.wireOp",EDGE,"E72.1");var subQ16=sQuery(id+"F12.wireOp",EDGE,"E74.1");var subQ18=sQuery(id+"F12.wireOp",EDGE,"E74.8");Q0=qUnion([makeQuery(id+"F12.imprint","IMPRINT",FACE,{"disambiguationData":[TD([[makeQuery(id+"F12.imprint","IMPRINT",EDGE,{"derivedFrom":subQ7}),1.0]])]}),makeQuery(id+"F12.imprint","IMPRINT",FACE,{"disambiguationData":[TD([[makeQuery(id+"F12.imprint","IMPRINT",EDGE,{"derivedFrom":subQ14}),1.0]])]}),makeQuery(id+"F12.imprint","IMPRINT",FACE,{"disambiguationData":[TD([[makeQuery(id+"F12.imprint","IMPRINT",EDGE,{"derivedFrom":subQ16}),1.0]])]}),makeQuery(id+"F12.imprint","IMPRINT",FACE,{"disambiguationData":[TD([[makeQuery(id+"F12.imprint","IMPRINT",EDGE,{"derivedFrom":subQ18}),-1.0]])]})]);}
            var Q1;
            Q1=makeQuery(id+"F5.boolean.opBoolean","SPLIT",FACE,{"disambiguationData":[TD([makeQuery(id+"F5.opExtrude","SWEPT_FACE",FACE,{"disambiguationData":[OSD([sQuery(id+"F4.wireOp",EDGE,"E41")])]})])],"derivedFrom":makeQuery(id+"F3.boolean.opBoolean","COPY",FACE,{"derivedFrom":makeQuery(id+"F3.opExtrude","CAP_FACE",FACE,{"disambiguationData":[OSD([sQuery(id+"F0.wireOp",EDGE,"E25.0"),sQuery(id+"F0.wireOp",EDGE,"E25.1"),sQuery(id+"F0.wireOp",EDGE,"E25.2"),sQuery(id+"F0.wireOp",EDGE,"E25.3"),sQuery(id+"F0.wireOp",EDGE,"E25.4"),sQuery(id+"F0.wireOp",EDGE,"E25.5"),sQuery(id+"F0.wireOp",EDGE,"E25.6"),sQuery(id+"F0.wireOp",EDGE,"E25.7")])],"isStart":false})})});
            extrude(context, id + "F13", {"entities" : qUnion([Q0]), "operationType" : NewBodyOperationType.REMOVE, "endBound" : BoundingType.UP_TO_SURFACE, "endBoundEntityFace" : qUnion([Q1]), "depth" : 25 * mm});
        }
        {
            var Q0;
            Q0=makeQuery(id+"F3.boolean.opBoolean","COPY",EDGE,{"derivedFrom":makeQuery(id+"F3.opExtrude","CAP_EDGE",EDGE,{"disambiguationData":[OSD([sQuery(id+"F0.wireOp",EDGE,"E25.6")])],"isStart":false})});
            var Q1;
            Q1=makeQuery(id+"F8.boolean.opBoolean","INTERSECT",EDGE,{"derivedFrom":[makeQuery(id+"F5.opExtrude","SWEPT_FACE",FACE,{"disambiguationData":[OSD([sQuery(id+"F4.wireOp",EDGE,"E30")])]}),makeQuery(id+"F8.opExtrude","CAP_FACE",FACE,{"disambiguationData":[OSD([sQuery(id+"F7.wireOp",EDGE,"E67")])],"isStart":false})]});
            var Q2;
            Q2=makeQuery(id+"F8.boolean.opBoolean","INTERSECT",EDGE,{"disambiguationData":[OD(1.0)],"derivedFrom":[makeQuery(id+"F5.opExtrude","SWEPT_FACE",FACE,{"disambiguationData":[OSD([sQuery(id+"F4.wireOp",EDGE,"E30")])]}),makeQuery(id+"F8.opExtrude","SWEPT_FACE",FACE,{"disambiguationData":[OSD([sQuery(id+"F7.wireOp",EDGE,"E67")])]})]});
            var Q3;
            {var subQ0=sQuery(id+"F4.wireOp",EDGE,"E30");Q3=makeQuery(id+"F8.boolean.opBoolean","SPLIT",EDGE,{"disambiguationData":[TD([makeQuery(id+"F5.opExtrude","SWEPT_FACE",FACE,{"disambiguationData":[OSD([sQuery(id+"F4.wireOp",EDGE,"E35.filletArc")])]})])],"derivedFrom":makeQuery(id+"F5.opExtrude","CAP_EDGE",EDGE,{"disambiguationData":[OSD([subQ0])],"isStart":false})});}
            var Q4;
            {var subQ0=sQuery(id+"F0.wireOp",EDGE,"E25.7");var subQ1=sQuery(id+"F0.wireOp",EDGE,"E25.1");var subQ2=sQuery(id+"F0.wireOp",EDGE,"E25.6");var subQ3=sQuery(id+"F0.wireOp",EDGE,"E25.5");var subQ4=sQuery(id+"F0.wireOp",EDGE,"E25.4");var subQ5=sQuery(id+"F0.wireOp",EDGE,"E25.0");var subQ6=sQuery(id+"F0.wireOp",EDGE,"E25.2");var subQ7=sQuery(id+"F0.wireOp",EDGE,"E25.3");Q4=makeQuery(id+"F8.boolean.opBoolean","INTERSECT",EDGE,{"derivedFrom":[makeQuery(id+"F5.boolean.opBoolean","SPLIT",FACE,{"disambiguationData":[TD([makeQuery(id+"F2.opExtrude","SWEPT_FACE",FACE,{"disambiguationData":[OSD([subQ5])]})])],"derivedFrom":makeQuery(id+"F3.boolean.opBoolean","COPY",FACE,{"derivedFrom":makeQuery(id+"F3.opExtrude","CAP_FACE",FACE,{"disambiguationData":[OSD([subQ5,subQ1,subQ6,subQ7,subQ4,subQ3,subQ2,subQ0])],"isStart":false})})}),makeQuery(id+"F8.opExtrude","SWEPT_FACE",FACE,{"disambiguationData":[OSD([sQuery(id+"F7.wireOp",EDGE,"E67")])]})]});}
            var Q5;
            Q5=makeQuery(id+"F8.boolean.opBoolean","INTERSECT",EDGE,{"disambiguationData":[OD(0.0)],"derivedFrom":[makeQuery(id+"F5.opExtrude","SWEPT_FACE",FACE,{"disambiguationData":[OSD([sQuery(id+"F4.wireOp",EDGE,"E30")])]}),makeQuery(id+"F8.opExtrude","SWEPT_FACE",FACE,{"disambiguationData":[OSD([sQuery(id+"F7.wireOp",EDGE,"E67")])]})]});
            fillet(context, id + "F14", {"entities" : qUnion([Q0, Q1, Q2, Q3, Q4, Q5]), "radius" : 3 * mm, "tangentPropagation" : true, "allowEdgeOverflow" : false});
        }
        {
            var Q0;
            Q0=makeQuery(id+"F1.opExtrude","CAP_EDGE",EDGE,{"disambiguationData":[OSD([sQuery(id+"F0.wireOp",EDGE,"E1.bottom")])],"isStart":false});
            fillet(context, id + "F15", {"entities" : qUnion([Q0]), "radius" : 2 * mm, "tangentPropagation" : true, "allowEdgeOverflow" : false});
        }
        {
            var Q0;
            {var subQ0=sQuery(id+"F0.wireOp",EDGE,"E21.filletArc");var subQ1=sQuery(id+"F0.wireOp",EDGE,"E7");var subQ2=sQuery(id+"F0.wireOp",EDGE,"E6");var subQ3=sQuery(id+"F0.wireOp",EDGE,"E5");var subQ4=sQuery(id+"F0.wireOp",EDGE,"E4");var subQ5=sQuery(id+"F0.wireOp",EDGE,"E22.filletArc");var subQ6=sQuery(id+"F0.wireOp",EDGE,"E1.bottom");var subQ7=sQuery(id+"F0.wireOp",EDGE,"E1.right");var subQ8=sQuery(id+"F0.wireOp",EDGE,"E1.top");var subQ9=sQuery(id+"F0.wireOp",EDGE,"E1.left");var subQ10=sQuery(id+"F0.wireOp",EDGE,"E23.filletArc");var subQ11=sQuery(id+"F0.wireOp",EDGE,"E24.filletArc");Q0=makeQuery(id+"F2.boolean.opBoolean","SPLIT",FACE,{"disambiguationData":[TD([makeQuery(id+"F1.opExtrude","SWEPT_FACE",FACE,{"disambiguationData":[OSD([subQ6])]})])],"derivedFrom":makeQuery(id+"F1.opExtrude","CAP_FACE",FACE,{"disambiguationData":[OSD([subQ6,subQ8,subQ9,subQ7,subQ4,subQ3,subQ2,subQ1,subQ0,subQ5,subQ10,subQ11])],"isStart":true})});}
            var sketch = newSketch(context, id + "F16", { "sketchPlane" : qUnion([Q0])});
            skLineSegment(sketch, "E79", {"start": v(0, 90) * mm, "end": v(0, 120) * mm, "construction": true});
            skCircle(sketch, "E80", {"center": v(0, 120) * mm, "radius": 6 * mm});
            skLineSegment(sketch, "E81", {"start": v(15, 108) * mm, "end": v(15, 120) * mm});
            skLineSegment(sketch, "E82", {"start": v(-15, 108) * mm, "end": v(-15, 120) * mm});
            skArc(sketch, "E83", {"start": v(15, 120) * mm, "mid": v(0, 135) * mm, "end": v(-15, 120) * mm});
            skLineSegment(sketch, "E84", {"start": v(33, 90) * mm, "end": v(15, 108) * mm});
            skLineSegment(sketch, "E85", {"start": v(-33, 90) * mm, "end": v(-15, 108) * mm});
            skLineSegment(sketch, "E86", {"start": v(-80, 0) * mm, "end": v(80, 0) * mm, "construction": true});
            skLineSegment(sketch, "E87.MirrorCS", {"start": v(-33, -90) * mm, "end": v(-15, -108) * mm});
            skLineSegment(sketch, "E88.MirrorCS", {"start": v(-15, -108) * mm, "end": v(-15, -120) * mm});
            skArc(sketch, "E89.MirrorCS", {"start": v(15, -120) * mm, "mid": v(0, -135) * mm, "end": v(-15, -120) * mm});
            skLineSegment(sketch, "E90.MirrorCS", {"start": v(15, -108) * mm, "end": v(15, -120) * mm});
            skLineSegment(sketch, "E91.MirrorCS", {"start": v(33, -90) * mm, "end": v(15, -108) * mm});
            skLineSegment(sketch, "E92.MirrorCS", {"start": v(0, -90) * mm, "end": v(0, -120) * mm, "construction": true});
            skCircle(sketch, "E93.MirrorC", {"center": v(0, -120) * mm, "radius": 6 * mm});
            skSolve(sketch);
        }
        {
            var Q0;
            Q0=makeQuery(id+"F16.imprint","IMPRINT",FACE,{"disambiguationData":[TD([[makeQuery(id+"F16.imprint","IMPRINT",EDGE,{"derivedFrom":sQuery(id+"F16.wireOp",EDGE,"E80")}),-1.0]])]});
            var Q1;
            Q1=makeQuery(id+"F16.imprint","IMPRINT",FACE,{"disambiguationData":[TD([[makeQuery(id+"F16.imprint","IMPRINT",EDGE,{"derivedFrom":makeQuery(id+"F1.opExtrude","CAP_EDGE",EDGE,{"disambiguationData":[OSD([sQuery(id+"F0.wireOp",EDGE,"E1.left")])],"isStart":true})}),-1.0]])]});
            var Q2;
            {var subQ0=sQuery(id+"F16.wireOp",EDGE,"E87.MirrorCS");Q2=makeQuery(id+"F16.imprint","IMPRINT",FACE,{"disambiguationData":[TD([[makeQuery(id+"F16.imprint","IMPRINT",EDGE,{"derivedFrom":subQ0}),1.0]])]});}
            var Q3;
            Q3=makeQuery(id+"F2.opExtrude","CAP_FACE",FACE,{"disambiguationData":[OSD([sQuery(id+"F0.wireOp",EDGE,"E12"),sQuery(id+"F0.wireOp",EDGE,"E13"),sQuery(id+"F0.wireOp",EDGE,"E14"),sQuery(id+"F0.wireOp",EDGE,"E15"),sQuery(id+"F0.wireOp",EDGE,"E17.filletArc"),sQuery(id+"F0.wireOp",EDGE,"E18.filletArc"),sQuery(id+"F0.wireOp",EDGE,"E19.filletArc"),sQuery(id+"F0.wireOp",EDGE,"E20.filletArc"),sQuery(id+"F0.wireOp",EDGE,"E25.0"),sQuery(id+"F0.wireOp",EDGE,"E25.1"),sQuery(id+"F0.wireOp",EDGE,"E25.2"),sQuery(id+"F0.wireOp",EDGE,"E25.3"),sQuery(id+"F0.wireOp",EDGE,"E25.4"),sQuery(id+"F0.wireOp",EDGE,"E25.5"),sQuery(id+"F0.wireOp",EDGE,"E25.6"),sQuery(id+"F0.wireOp",EDGE,"E25.7")])],"isStart":false});
            extrude(context, id + "F17", {"entities" : qUnion([Q0, Q1, Q2]), "endBound" : BoundingType.UP_TO_SURFACE, "endBoundEntityFace" : qUnion([Q3]), "depth" : 25 * mm});
        }
    });
